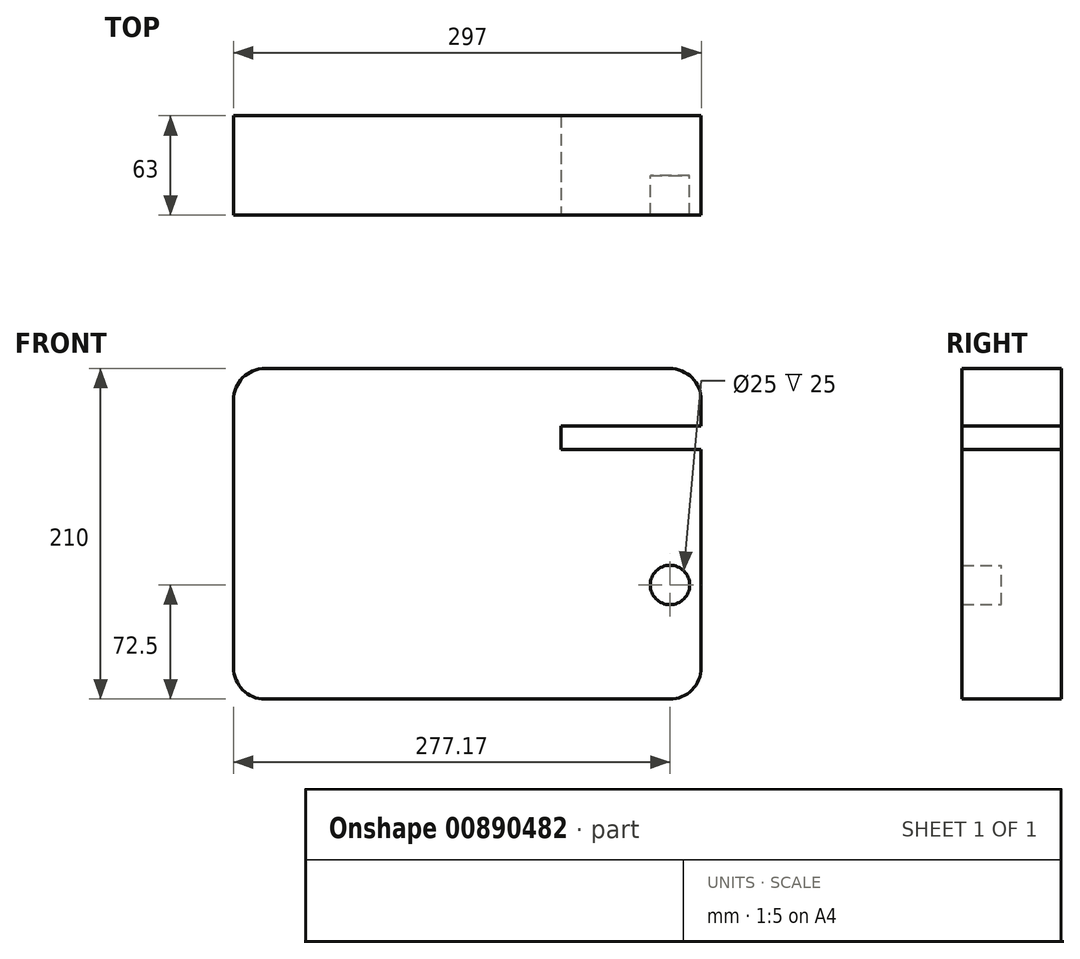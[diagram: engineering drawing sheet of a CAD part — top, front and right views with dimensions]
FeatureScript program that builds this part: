
annotation { "Feature Type Name" : "Feature", "Feature Type Description" : "" }
export const myFeature = defineFeature(function(context is Context, id is Id, definition is map)
    precondition{}
    {
        {
            var Q0;
            Q0=qCreatedBy(makeId("Front.planeOp"),FACE);
            var sketch = newSketch(context, id + "F0", { "sketchPlane" : qUnion([Q0])});
            skLineSegment(sketch, "E0.bottom", {"start": v(-144.67, 210) * mm, "end": v(112.33, 210) * mm});
            skLineSegment(sketch, "E0.top", {"start": v(-144.67, 0) * mm, "end": v(112.33, 0) * mm});
            skLineSegment(sketch, "E0.left", {"start": v(-164.67, 190) * mm, "end": v(-164.67, 20) * mm});
            skLineSegment(sketch, "E0.right", {"start": v(132.33, 190) * mm, "end": v(132.33, 20) * mm});
            skPoint(sketch, "E1.visualSharp", {"position": v(-164.67, 210) * mm});
            skArc(sketch, "E1.filletArc", {"start": v(-144.67, 210) * mm, "mid": v(-158.82, 204.14) * mm, "end": v(-164.67, 190) * mm});
            skPoint(sketch, "E2.visualSharp", {"position": v(132.33, 210) * mm});
            skArc(sketch, "E2.filletArc", {"start": v(132.33, 190) * mm, "mid": v(126.47, 204.14) * mm, "end": v(112.33, 210) * mm});
            skPoint(sketch, "E3.visualSharp", {"position": v(-164.67, 0) * mm});
            skArc(sketch, "E3.filletArc", {"start": v(-164.67, 20) * mm, "mid": v(-158.82, 5.86) * mm, "end": v(-144.67, 0) * mm});
            skPoint(sketch, "E4.visualSharp", {"position": v(132.33, 0) * mm});
            skArc(sketch, "E4.filletArc", {"start": v(112.33, 0) * mm, "mid": v(126.47, 5.86) * mm, "end": v(132.33, 20) * mm});
            skSolve(sketch);
        }
        {
            var Q0;
            Q0=makeQuery(id+"F0.imprint","IMPRINT",FACE,{"disambiguationData":[TD([[makeQuery(id+"F0.imprint","IMPRINT",EDGE,{"derivedFrom":sQuery(id+"F0.wireOp",EDGE,"E0.bottom")}),-1.0]])]});
            extrude(context, id + "F1", {"entities" : qUnion([Q0]), "depth" : 13 * mm, "offsetDistance" : 25 * mm});
        }
        {
            var Q0;
            Q0 = qSketchRegion(id + "F0", true);
            var Q1;
            Q1=makeQuery(id+"F1.opExtrude","CAP_FACE",FACE,{"disambiguationData":[OSD([sQuery(id+"F0.wireOp",EDGE,"E0.bottom"),sQuery(id+"F0.wireOp",EDGE,"E0.top"),sQuery(id+"F0.wireOp",EDGE,"E0.left"),sQuery(id+"F0.wireOp",EDGE,"E0.right"),sQuery(id+"F0.wireOp",EDGE,"E1.filletArc"),sQuery(id+"F0.wireOp",EDGE,"E2.filletArc"),sQuery(id+"F0.wireOp",EDGE,"E3.filletArc"),sQuery(id+"F0.wireOp",EDGE,"E4.filletArc")])],"isStart":false});
            extrude(context, id + "F2", {"entities" : qUnion([Q0, Q1]), "operationType" : NewBodyOperationType.ADD, "depth" : 25 * mm, "offsetDistance" : 25 * mm});
        }
        {
            var Q0;
            {var subQ0=sQuery(id+"F0.wireOp",EDGE,"E4.filletArc");var subQ1=sQuery(id+"F0.wireOp",EDGE,"E3.filletArc");var subQ2=sQuery(id+"F0.wireOp",EDGE,"E2.filletArc");var subQ3=sQuery(id+"F0.wireOp",EDGE,"E1.filletArc");var subQ4=sQuery(id+"F0.wireOp",EDGE,"E0.right");var subQ5=sQuery(id+"F0.wireOp",EDGE,"E0.left");var subQ6=sQuery(id+"F0.wireOp",EDGE,"E0.top");var subQ7=sQuery(id+"F0.wireOp",EDGE,"E0.bottom");Q0=makeQuery(id+"F2.opExtrude","CAP_FACE",FACE,{"disambiguationData":[OSD([subQ7,subQ6,subQ5,subQ4,subQ3,subQ2,subQ1,subQ0]),TDD([makeQuery(id+"F1.opExtrude","CAP_FACE",FACE,{"disambiguationData":[OSD([subQ7,subQ6,subQ5,subQ4,subQ3,subQ2,subQ1,subQ0])],"isStart":false})])],"isStart":false});}
            var sketch = newSketch(context, id + "F3", { "sketchPlane" : qUnion([Q0])});
            skLineSegment(sketch, "E5.bottom", {"start": v(153.2, 173.47) * mm, "end": v(43.2, 173.47) * mm});
            skLineSegment(sketch, "E5.top", {"start": v(153.2, 158.47) * mm, "end": v(43.2, 158.47) * mm});
            skLineSegment(sketch, "E5.left", {"start": v(153.2, 173.47) * mm, "end": v(153.2, 158.47) * mm});
            skLineSegment(sketch, "E5.right", {"start": v(43.2, 173.47) * mm, "end": v(43.2, 158.47) * mm});
            skSolve(sketch);
        }
        {
            var Q0;
            Q0 = qSketchRegion(id + "F3", true);
            extrude(context, id + "F4", {"entities" : qUnion([Q0]), "operationType" : NewBodyOperationType.REMOVE, "oppositeDirection" : true, "depth" : 25 * mm, "offsetDistance" : 25 * mm});
        }
        {
            var Q0;
            Q0=makeQuery(id+"F4.boolean.opBoolean","COPY",FACE,{"derivedFrom":makeQuery(id+"F4.opExtrude","CAP_FACE",FACE,{"disambiguationData":[OSD([sQuery(id+"F3.wireOp",EDGE,"E5.bottom"),sQuery(id+"F3.wireOp",EDGE,"E5.top"),sQuery(id+"F3.wireOp",EDGE,"E5.left"),sQuery(id+"F3.wireOp",EDGE,"E5.right")])],"isStart":false})});
            extrude(context, id + "F5", {"entities" : qUnion([Q0]), "operationType" : NewBodyOperationType.REMOVE, "oppositeDirection" : true, "depth" : 25 * mm, "offsetDistance" : 25 * mm});
        }
        {
            var Q0;
            {var subQ0=sQuery(id+"F0.wireOp",EDGE,"E4.filletArc");var subQ1=sQuery(id+"F0.wireOp",EDGE,"E3.filletArc");var subQ2=sQuery(id+"F0.wireOp",EDGE,"E2.filletArc");var subQ3=sQuery(id+"F0.wireOp",EDGE,"E1.filletArc");var subQ4=sQuery(id+"F0.wireOp",EDGE,"E0.right");var subQ5=sQuery(id+"F0.wireOp",EDGE,"E0.left");var subQ6=sQuery(id+"F0.wireOp",EDGE,"E0.top");var subQ7=sQuery(id+"F0.wireOp",EDGE,"E0.bottom");Q0=makeQuery(id+"F2.opExtrude","CAP_FACE",FACE,{"disambiguationData":[OSD([subQ7,subQ6,subQ5,subQ4,subQ3,subQ2,subQ1,subQ0]),TDD([makeQuery(id+"F1.opExtrude","CAP_FACE",FACE,{"disambiguationData":[OSD([subQ7,subQ6,subQ5,subQ4,subQ3,subQ2,subQ1,subQ0])],"isStart":false})])],"isStart":false});}
            var sketch = newSketch(context, id + "F6", { "sketchPlane" : qUnion([Q0])});
            skCircle(sketch, "E6", {"center": v(2.5, 72.5) * mm, "radius": 12.5 * mm});
            skCircle(sketch, "E7", {"center": v(57.5, 72.5) * mm, "radius": 12.5 * mm});
            skCircle(sketch, "E8", {"center": v(112.5, 72.5) * mm, "radius": 12.5 * mm});
            skSolve(sketch);
        }
        {
            var Q0;
            Q0=makeQuery(id+"F6.imprint","IMPRINT",FACE,{"disambiguationData":[TD([[makeQuery(id+"F6.imprint","IMPRINT",EDGE,{"derivedFrom":sQuery(id+"F6.wireOp",EDGE,"E6")}),1.0]])]});
            var Q1;
            Q1=makeQuery(id+"F6.imprint","IMPRINT",FACE,{"disambiguationData":[TD([[makeQuery(id+"F6.imprint","IMPRINT",EDGE,{"derivedFrom":sQuery(id+"F6.wireOp",EDGE,"E7")}),1.0]])]});
            var Q2;
            Q2=makeQuery(id+"F6.imprint","IMPRINT",FACE,{"disambiguationData":[TD([[makeQuery(id+"F6.imprint","IMPRINT",EDGE,{"derivedFrom":sQuery(id+"F6.wireOp",EDGE,"E6")}),-1.0]])]});
            extrude(context, id + "F7", {"entities" : qUnion([Q0, Q1, Q2]), "operationType" : NewBodyOperationType.ADD, "depth" : 25 * mm, "offsetDistance" : 25 * mm});
        }
    });
